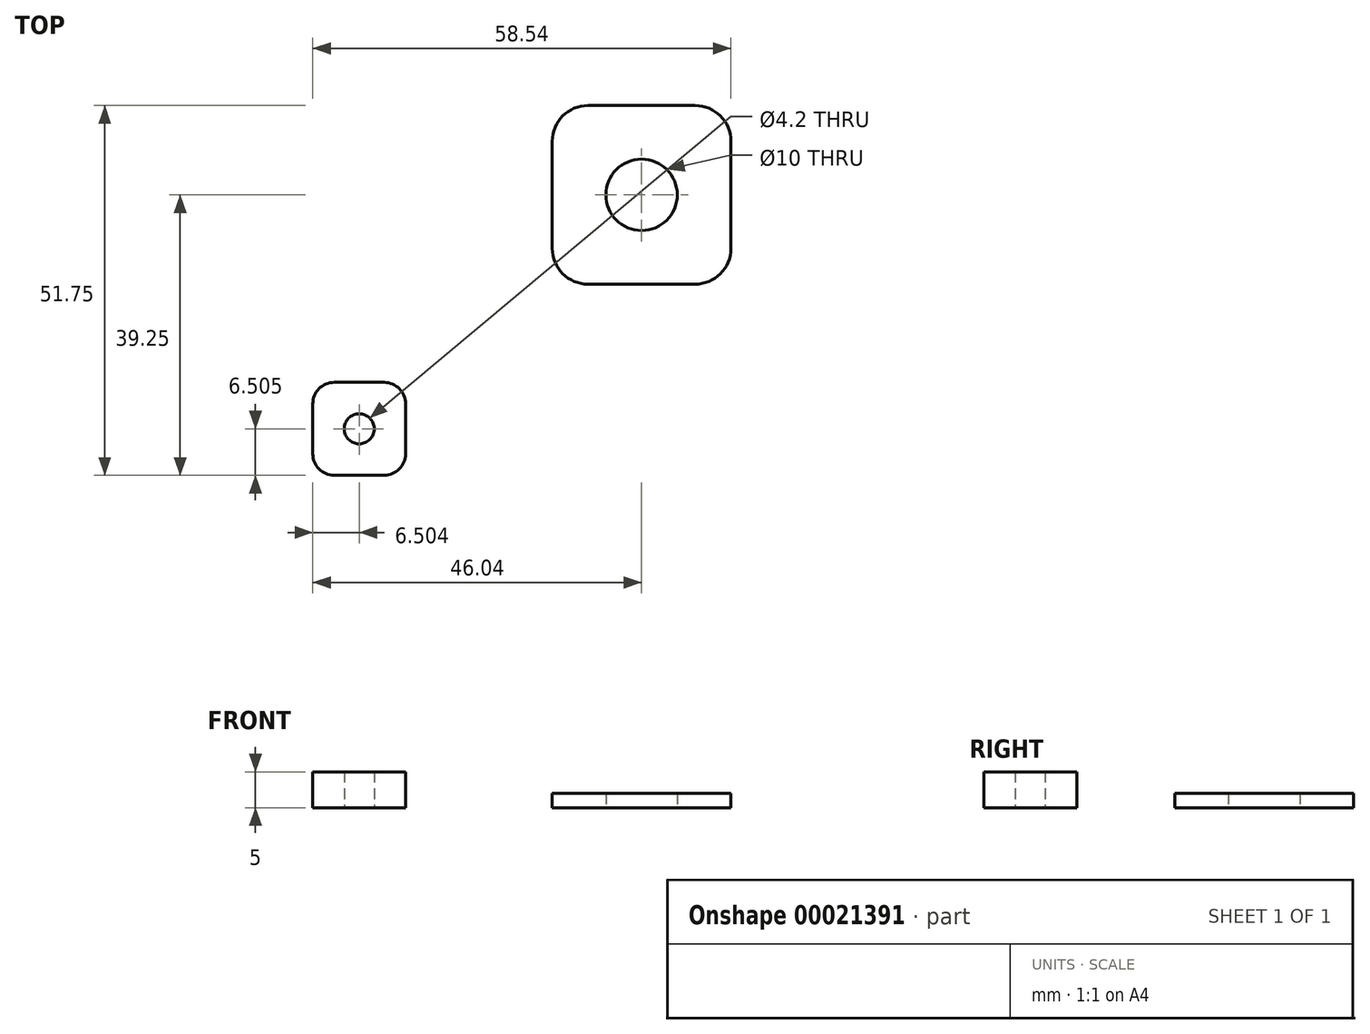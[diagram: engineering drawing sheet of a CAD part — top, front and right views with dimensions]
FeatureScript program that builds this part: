
annotation { "Feature Type Name" : "Feature", "Feature Type Description" : "" }
export const myFeature = defineFeature(function(context is Context, id is Id, definition is map)
    precondition{}
    {
        {
            var Q0;
            Q0=qCreatedBy(makeId("Top.planeOp"),FACE);
            var sketch = newSketch(context, id + "F0", { "sketchPlane" : qUnion([Q0])});
            skLineSegment(sketch, "E0.rect.bottom", {"start": v(-7.5, 12.5) * mm, "end": v(7.5, 12.5) * mm});
            skLineSegment(sketch, "E0.rect.top", {"start": v(-7.5, -12.5) * mm, "end": v(7.5, -12.5) * mm});
            skLineSegment(sketch, "E0.rect.left", {"start": v(-12.5, 7.5) * mm, "end": v(-12.5, -7.5) * mm});
            skLineSegment(sketch, "E0.rect.right", {"start": v(12.5, 7.5) * mm, "end": v(12.5, -7.5) * mm});
            skPoint(sketch, "E0.rect.middle", {"position": v(0, 0) * mm});
            skPoint(sketch, "E1.visualSharp", {"position": v(-12.5, 12.5) * mm});
            skArc(sketch, "E1.filletArc", {"start": v(-7.5, 12.5) * mm, "mid": v(-11.04, 11.04) * mm, "end": v(-12.5, 7.5) * mm});
            skPoint(sketch, "E2.visualSharp", {"position": v(12.5, 12.5) * mm});
            skArc(sketch, "E2.filletArc", {"start": v(12.5, 7.5) * mm, "mid": v(11.04, 11.04) * mm, "end": v(7.5, 12.5) * mm});
            skPoint(sketch, "E3.visualSharp", {"position": v(12.5, -12.5) * mm});
            skArc(sketch, "E3.filletArc", {"start": v(7.5, -12.5) * mm, "mid": v(11.04, -11.04) * mm, "end": v(12.5, -7.5) * mm});
            skPoint(sketch, "E4.visualSharp", {"position": v(-12.5, -12.5) * mm});
            skArc(sketch, "E4.filletArc", {"start": v(-12.5, -7.5) * mm, "mid": v(-11.04, -11.04) * mm, "end": v(-7.5, -12.5) * mm});
            skCircle(sketch, "E5", {"center": v(0, 0) * mm, "radius": 5 * mm});
            skSolve(sketch);
        }
        {
            var Q0;
            Q0 = qSketchRegion(id + "F0", true);
            extrude(context, id + "F1", {"entities" : qUnion([Q0]), "depth" : 2 * mm});
        }
        {
            var Q0;
            Q0=qCreatedBy(makeId("Top.planeOp"),FACE);
            var sketch = newSketch(context, id + "F2", { "sketchPlane" : qUnion([Q0])});
            skPoint(sketch, "E6", {"position": v(-39.54, -32.75) * mm});
            skLineSegment(sketch, "E7.rect.bottom", {"start": v(-36.04, -39.25) * mm, "end": v(-43.04, -39.25) * mm});
            skLineSegment(sketch, "E7.rect.top", {"start": v(-36.04, -26.25) * mm, "end": v(-43.04, -26.25) * mm});
            skLineSegment(sketch, "E7.rect.left", {"start": v(-33.04, -36.25) * mm, "end": v(-33.04, -29.25) * mm});
            skLineSegment(sketch, "E7.rect.right", {"start": v(-46.04, -36.25) * mm, "end": v(-46.04, -29.25) * mm});
            skCircle(sketch, "E8", {"center": v(-39.54, -32.75) * mm, "radius": 2.1 * mm});
            skPoint(sketch, "E9.visualSharp", {"position": v(-46.04, -26.25) * mm});
            skArc(sketch, "E9.filletArc", {"start": v(-43.04, -26.25) * mm, "mid": v(-45.16, -27.12) * mm, "end": v(-46.04, -29.25) * mm});
            skPoint(sketch, "E10.visualSharp", {"position": v(-33.04, -26.25) * mm});
            skArc(sketch, "E10.filletArc", {"start": v(-33.04, -29.25) * mm, "mid": v(-33.91, -27.12) * mm, "end": v(-36.04, -26.25) * mm});
            skPoint(sketch, "E11.visualSharp", {"position": v(-33.04, -39.25) * mm});
            skArc(sketch, "E11.filletArc", {"start": v(-36.04, -39.25) * mm, "mid": v(-33.91, -38.37) * mm, "end": v(-33.04, -36.25) * mm});
            skPoint(sketch, "E12.visualSharp", {"position": v(-46.04, -39.25) * mm});
            skArc(sketch, "E12.filletArc", {"start": v(-46.04, -36.25) * mm, "mid": v(-45.16, -38.37) * mm, "end": v(-43.04, -39.25) * mm});
            skSolve(sketch);
        }
        {
            var Q0;
            Q0 = qSketchRegion(id + "F2", true);
            extrude(context, id + "F3", {"entities" : qUnion([Q0]), "depth" : 5 * mm});
        }
    });
